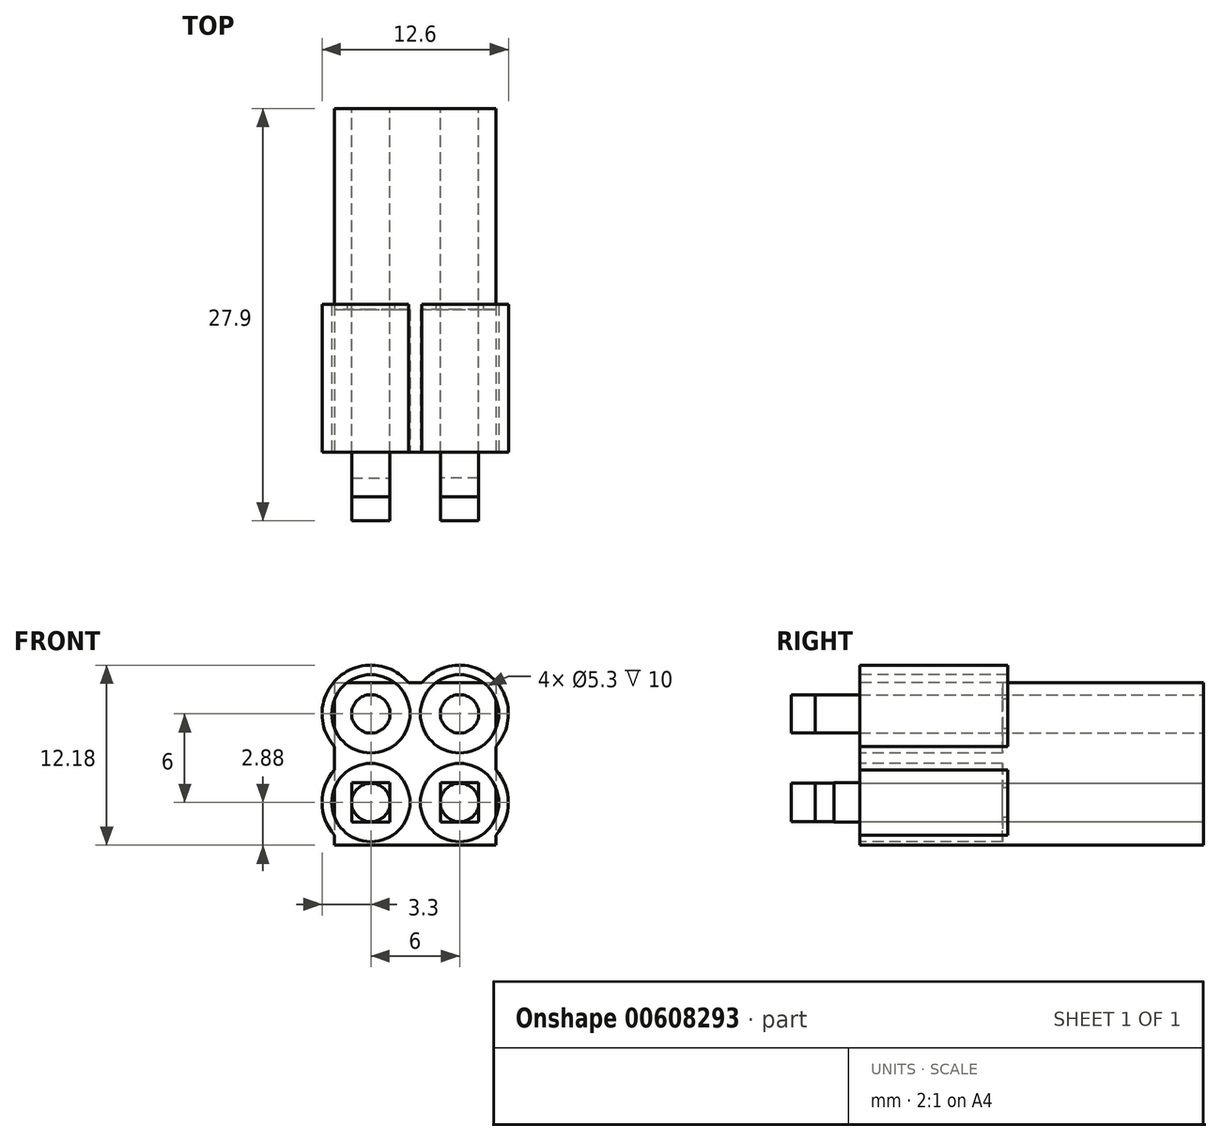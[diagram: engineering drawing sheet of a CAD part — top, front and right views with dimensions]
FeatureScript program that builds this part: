
annotation { "Feature Type Name" : "Feature", "Feature Type Description" : "" }
export const myFeature = defineFeature(function(context is Context, id is Id, definition is map)
    precondition{}
    {
        {
            var Q0;
            Q0=qCreatedBy(makeId("Front.planeOp"),FACE);
            var sketch = newSketch(context, id + "F0", { "sketchPlane" : qUnion([Q0])});
            skLineSegment(sketch, "E0.bottom", {"start": v(-5.45, 6.3) * mm, "end": v(5.45, 6.3) * mm});
            skLineSegment(sketch, "E0.top", {"start": v(-5.45, -6.3) * mm, "end": v(5.45, -6.3) * mm});
            skLineSegment(sketch, "E0.left", {"start": v(-5.45, 6.3) * mm, "end": v(-5.45, -6.3) * mm});
            skLineSegment(sketch, "E0.right", {"start": v(5.45, 6.3) * mm, "end": v(5.45, -6.3) * mm});
            skPoint(sketch, "E0.middle", {"position": v(0, 0) * mm});
            skSolve(sketch);
        }
        {
            var Q0;
            Q0 = qSketchRegion(id + "F0", true);
            extrude(context, id + "F1", {"entities" : qUnion([Q0]), "depth" : 23.26 * mm, "offsetDistance" : 25 * mm});
        }
        {
            var Q0;
            {var subQ0=makeQuery(id+"F7.opExtrude","SWEPT_FACE",FACE,{"disambiguationData":[OSD([sQuery(id+"F6.wireOp",EDGE,"E14")])]});var subQ1=sQuery(id+"F0.wireOp",EDGE,"E0.left");var subQ2=makeQuery(id+"F1.opExtrude","SWEPT_FACE",FACE,{"disambiguationData":[OSD([subQ1])]});var subQ3=sQuery(id+"F0.wireOp",EDGE,"E0.right");var subQ4=makeQuery(id+"F1.opExtrude","SWEPT_FACE",FACE,{"disambiguationData":[OSD([subQ3])]});var subQ5=sQuery(id+"F0.wireOp",EDGE,"E0.bottom");var subQ6=makeQuery(id+"F1.opExtrude","SWEPT_FACE",FACE,{"disambiguationData":[OSD([subQ5])]});var subQ7=makeQuery(id+"F7.opExtrude","SWEPT_FACE",FACE,{"disambiguationData":[OSD([sQuery(id+"F6.wireOp",EDGE,"E15")])]});var subQ8=makeQuery(id+"F1.opExtrude","CAP_FACE",FACE,{"disambiguationData":[OSD([subQ5,sQuery(id+"F0.wireOp",EDGE,"E0.top"),subQ1,subQ3])],"isStart":true});Q0=makeQuery(id+"F9.boolean.opBoolean","MERGE",FACE,{"derivedFrom":[makeQuery(id+"F7.boolean.opBoolean","SPLIT",FACE,{"disambiguationData":[TD([subQ6,subQ2,subQ0])],"derivedFrom":subQ8}),makeQuery(id+"F7.boolean.opBoolean","SPLIT",FACE,{"disambiguationData":[TD([subQ6,subQ4,subQ7])],"derivedFrom":subQ8}),makeQuery(id+"F7.boolean.opBoolean","SPLIT",FACE,{"disambiguationData":[TD([subQ6,subQ2,subQ4,subQ0,subQ7,makeQuery(id+"F7.opExtrude","SWEPT_FACE",FACE,{"disambiguationData":[OSD([sQuery(id+"F6.wireOp",EDGE,"E16")])]}),makeQuery(id+"F7.opExtrude","SWEPT_FACE",FACE,{"disambiguationData":[OSD([sQuery(id+"F6.wireOp",EDGE,"E17")])]}),makeQuery(id+"F7.opExtrude","SWEPT_FACE",FACE,{"disambiguationData":[OSD([sQuery(id+"F6.wireOp",EDGE,"E18.top")])]})])],"derivedFrom":subQ8}),makeQuery(id+"F9.opExtrude","CAP_FACE",FACE,{"disambiguationData":[OSD([sQuery(id+"F8.wireOp",EDGE,"E19.bottom"),sQuery(id+"F8.wireOp",EDGE,"E19.top"),sQuery(id+"F8.wireOp",EDGE,"E19.left"),sQuery(id+"F8.wireOp",EDGE,"E19.right")])],"isStart":true})]});}
            var sketch = newSketch(context, id + "F2", { "sketchPlane" : qUnion([Q0])});
            skLineSegment(sketch, "E1.bottom", {"start": v(-4.3, -0.47) * mm, "end": v(-1.7, -0.47) * mm});
            skLineSegment(sketch, "E1.top", {"start": v(-4.3, -3.13) * mm, "end": v(-1.7, -3.13) * mm});
            skLineSegment(sketch, "E1.left", {"start": v(-4.3, -0.47) * mm, "end": v(-4.3, -3.13) * mm});
            skLineSegment(sketch, "E1.right", {"start": v(-1.7, -0.47) * mm, "end": v(-1.7, -3.13) * mm});
            skPoint(sketch, "E1.middle", {"position": v(-3, -1.8) * mm});
            skLineSegment(sketch, "E2.MirrorCS", {"start": v(4.3, -3.13) * mm, "end": v(1.7, -3.13) * mm});
            skLineSegment(sketch, "E3.MirrorCS", {"start": v(4.3, -0.47) * mm, "end": v(4.3, -3.13) * mm});
            skLineSegment(sketch, "E4.MirrorCS", {"start": v(4.3, -0.47) * mm, "end": v(1.7, -0.47) * mm});
            skLineSegment(sketch, "E5.MirrorCS", {"start": v(1.7, -0.47) * mm, "end": v(1.7, -3.13) * mm});
            skPoint(sketch, "E6.MirrorP", {"position": v(3, -1.8) * mm});
            skSolve(sketch);
        }
        {
            var Q0;
            Q0 = qSketchRegion(id + "F2", true);
            extrude(context, id + "F3", {"entities" : qUnion([Q0]), "oppositeDirection" : true, "depth" : 25 * mm, "offsetDistance" : 25 * mm});
        }
        {
            var Q0;
            Q0=makeQuery(id+"F1.opExtrude","CAP_FACE",FACE,{"disambiguationData":[OSD([sQuery(id+"F0.wireOp",EDGE,"E0.bottom"),sQuery(id+"F0.wireOp",EDGE,"E0.top"),sQuery(id+"F0.wireOp",EDGE,"E0.left"),sQuery(id+"F0.wireOp",EDGE,"E0.right")])],"isStart":false});
            var sketch = newSketch(context, id + "F4", { "sketchPlane" : qUnion([Q0])});
            skArc(sketch, "E7", {"start": v(0, 5.57) * mm, "mid": v(-5.33, 6.53) * mm, "end": v(-4.37, 1.2) * mm});
            skArc(sketch, "E8", {"start": v(4.37, 1.2) * mm, "mid": v(5.33, 6.53) * mm, "end": v(0, 5.57) * mm});
            skLineSegment(sketch, "E9", {"start": v(-3, 4.2) * mm, "end": v(-3, 1.2) * mm});
            skArc(sketch, "E10.MirrorC", {"start": v(-4.37, 1.2) * mm, "mid": v(-5.33, 6.53) * mm, "end": v(0, 5.57) * mm});
            skArc(sketch, "E11.MirrorC", {"start": v(4.37, 1.2) * mm, "mid": v(5.33, -4.13) * mm, "end": v(0, -3.17) * mm});
            skArc(sketch, "E12.trimOffspring", {"start": v(0, -3.17) * mm, "mid": v(-5.33, -4.13) * mm, "end": v(-4.37, 1.2) * mm});
            skPoint(sketch, "E13.end.orphan", {"position": v(-5.45, -1.8) * mm});
            skSolve(sketch);
        }
        {
            var Q0;
            Q0 = qSketchRegion(id + "F4", true);
            extrude(context, id + "F5", {"entities" : qUnion([Q0]), "operationType" : NewBodyOperationType.ADD, "oppositeDirection" : true, "depth" : 10 * mm, "offsetDistance" : 25 * mm});
        }
        {
            var Q0;
            Q0=makeQuery(id+"F5.boolean.opBoolean","MERGE",FACE,{"derivedFrom":[makeQuery(id+"F1.opExtrude","CAP_FACE",FACE,{"disambiguationData":[OSD([sQuery(id+"F0.wireOp",EDGE,"E0.bottom"),sQuery(id+"F0.wireOp",EDGE,"E0.top"),sQuery(id+"F0.wireOp",EDGE,"E0.left"),sQuery(id+"F0.wireOp",EDGE,"E0.right")])],"isStart":false}),makeQuery(id+"F5.opExtrude","CAP_FACE",FACE,{"disambiguationData":[OSD([sQuery(id+"F4.wireOp",EDGE,"E8"),sQuery(id+"F4.wireOp",EDGE,"E10.MirrorC"),sQuery(id+"F4.wireOp",EDGE,"E11.MirrorC"),sQuery(id+"F4.wireOp",EDGE,"E12.trimOffspring")])],"isStart":true})]});
            var sketch = newSketch(context, id + "F6", { "sketchPlane" : qUnion([Q0])});
            skCircle(sketch, "E14", {"center": v(-3, 4.2) * mm, "radius": 2.65 * mm});
            skCircle(sketch, "E15", {"center": v(3, 4.2) * mm, "radius": 2.65 * mm});
            skCircle(sketch, "E16", {"center": v(3, -1.8) * mm, "radius": 2.65 * mm});
            skCircle(sketch, "E17", {"center": v(-3, -1.8) * mm, "radius": 2.65 * mm});
            skLineSegment(sketch, "E18.bottom", {"start": v(5.45, -6.3) * mm, "end": v(-5.45, -6.3) * mm});
            skLineSegment(sketch, "E18.top", {"start": v(5.45, -4.68) * mm, "end": v(-5.45, -4.68) * mm});
            skLineSegment(sketch, "E18.left", {"start": v(5.45, -6.3) * mm, "end": v(5.45, -4.68) * mm});
            skLineSegment(sketch, "E18.right", {"start": v(-5.45, -6.3) * mm, "end": v(-5.45, -4.68) * mm});
            skSolve(sketch);
        }
        {
            var Q0;
            Q0 = qSketchRegion(id + "F6", true);
            extrude(context, id + "F7", {"entities" : qUnion([Q0]), "operationType" : NewBodyOperationType.REMOVE, "endBound" : BoundingType.THROUGH_ALL, "oppositeDirection" : true, "depth" : 25 * mm, "offsetDistance" : 25 * mm});
        }
        {
            var Q0;
            {var subQ0=sQuery(id+"F0.wireOp",EDGE,"E0.left");var subQ1=sQuery(id+"F0.wireOp",EDGE,"E0.right");var subQ2=sQuery(id+"F0.wireOp",EDGE,"E0.bottom");Q0=makeQuery(id+"F7.boolean.opBoolean","SPLIT",FACE,{"disambiguationData":[TD([makeQuery(id+"F1.opExtrude","SWEPT_FACE",FACE,{"disambiguationData":[OSD([subQ2])]}),makeQuery(id+"F1.opExtrude","SWEPT_FACE",FACE,{"disambiguationData":[OSD([subQ0])]}),makeQuery(id+"F1.opExtrude","SWEPT_FACE",FACE,{"disambiguationData":[OSD([subQ1])]}),makeQuery(id+"F7.opExtrude","SWEPT_FACE",FACE,{"disambiguationData":[OSD([sQuery(id+"F6.wireOp",EDGE,"E14")])]}),makeQuery(id+"F7.opExtrude","SWEPT_FACE",FACE,{"disambiguationData":[OSD([sQuery(id+"F6.wireOp",EDGE,"E15")])]}),makeQuery(id+"F7.opExtrude","SWEPT_FACE",FACE,{"disambiguationData":[OSD([sQuery(id+"F6.wireOp",EDGE,"E16")])]}),makeQuery(id+"F7.opExtrude","SWEPT_FACE",FACE,{"disambiguationData":[OSD([sQuery(id+"F6.wireOp",EDGE,"E17")])]}),makeQuery(id+"F7.opExtrude","SWEPT_FACE",FACE,{"disambiguationData":[OSD([sQuery(id+"F6.wireOp",EDGE,"E18.top")])]})])],"derivedFrom":makeQuery(id+"F1.opExtrude","CAP_FACE",FACE,{"disambiguationData":[OSD([subQ2,sQuery(id+"F0.wireOp",EDGE,"E0.top"),subQ0,subQ1])],"isStart":true})});}
            var sketch = newSketch(context, id + "F8", { "sketchPlane" : qUnion([Q0])});
            skLineSegment(sketch, "E19.bottom", {"start": v(5.45, -4.68) * mm, "end": v(-5.45, -4.68) * mm});
            skLineSegment(sketch, "E19.top", {"start": v(5.45, 6.3) * mm, "end": v(-5.45, 6.3) * mm});
            skLineSegment(sketch, "E19.left", {"start": v(5.45, -4.68) * mm, "end": v(5.45, 6.3) * mm});
            skLineSegment(sketch, "E19.right", {"start": v(-5.45, -4.68) * mm, "end": v(-5.45, 6.3) * mm});
            skSolve(sketch);
        }
        {
            var Q0;
            Q0 = qSketchRegion(id + "F8", true);
            extrude(context, id + "F9", {"entities" : qUnion([Q0]), "operationType" : NewBodyOperationType.ADD, "oppositeDirection" : true, "depth" : 13.6 * mm, "offsetDistance" : 25 * mm});
        }
        {
            var Q0;
            Q0=makeQuery(id+"F5.boolean.opBoolean","MERGE",FACE,{"derivedFrom":[makeQuery(id+"F1.opExtrude","CAP_FACE",FACE,{"disambiguationData":[OSD([sQuery(id+"F0.wireOp",EDGE,"E0.bottom"),sQuery(id+"F0.wireOp",EDGE,"E0.top"),sQuery(id+"F0.wireOp",EDGE,"E0.left"),sQuery(id+"F0.wireOp",EDGE,"E0.right")])],"isStart":false}),makeQuery(id+"F5.opExtrude","CAP_FACE",FACE,{"disambiguationData":[OSD([sQuery(id+"F4.wireOp",EDGE,"E8"),sQuery(id+"F4.wireOp",EDGE,"E10.MirrorC"),sQuery(id+"F4.wireOp",EDGE,"E11.MirrorC"),sQuery(id+"F4.wireOp",EDGE,"E12.trimOffspring")])],"isStart":true})]});
            var sketch = newSketch(context, id + "F10", { "sketchPlane" : qUnion([Q0])});
            skPoint(sketch, "E20", {"position": v(-3, -1.8) * mm});
            skCircle(sketch, "E21", {"center": v(-3, -1.8) * mm, "radius": 1.3 * mm});
            skCircle(sketch, "E22", {"center": v(-3, 4.2) * mm, "radius": 1.3 * mm});
            skPoint(sketch, "E23", {"position": v(3, -1.8) * mm});
            skCircle(sketch, "E24", {"center": v(3, -1.8) * mm, "radius": 1.3 * mm});
            skCircle(sketch, "E25", {"center": v(3, 4.2) * mm, "radius": 1.3 * mm});
            skSolve(sketch);
        }
        {
            var Q0;
            Q0 = qSketchRegion(id + "F10", true);
            extrude(context, id + "F11", {"entities" : qUnion([Q0]), "depth" : 3 * mm, "offsetDistance" : 25 * mm});
        }
        {
            var Q0;
            {var subQ0=makeQuery(id+"F7.opExtrude","SWEPT_FACE",FACE,{"disambiguationData":[OSD([sQuery(id+"F6.wireOp",EDGE,"E14")])]});var subQ1=sQuery(id+"F0.wireOp",EDGE,"E0.left");var subQ2=makeQuery(id+"F1.opExtrude","SWEPT_FACE",FACE,{"disambiguationData":[OSD([subQ1])]});var subQ3=sQuery(id+"F0.wireOp",EDGE,"E0.right");var subQ4=makeQuery(id+"F1.opExtrude","SWEPT_FACE",FACE,{"disambiguationData":[OSD([subQ3])]});var subQ5=sQuery(id+"F0.wireOp",EDGE,"E0.bottom");var subQ6=makeQuery(id+"F1.opExtrude","SWEPT_FACE",FACE,{"disambiguationData":[OSD([subQ5])]});var subQ7=makeQuery(id+"F7.opExtrude","SWEPT_FACE",FACE,{"disambiguationData":[OSD([sQuery(id+"F6.wireOp",EDGE,"E15")])]});var subQ8=makeQuery(id+"F1.opExtrude","CAP_FACE",FACE,{"disambiguationData":[OSD([subQ5,sQuery(id+"F0.wireOp",EDGE,"E0.top"),subQ1,subQ3])],"isStart":true});Q0=makeQuery(id+"F9.boolean.opBoolean","MERGE",FACE,{"derivedFrom":[makeQuery(id+"F7.boolean.opBoolean","SPLIT",FACE,{"disambiguationData":[TD([subQ6,subQ2,subQ0])],"derivedFrom":subQ8}),makeQuery(id+"F7.boolean.opBoolean","SPLIT",FACE,{"disambiguationData":[TD([subQ6,subQ4,subQ7])],"derivedFrom":subQ8}),makeQuery(id+"F7.boolean.opBoolean","SPLIT",FACE,{"disambiguationData":[TD([subQ6,subQ2,subQ4,subQ0,subQ7,makeQuery(id+"F7.opExtrude","SWEPT_FACE",FACE,{"disambiguationData":[OSD([sQuery(id+"F6.wireOp",EDGE,"E16")])]}),makeQuery(id+"F7.opExtrude","SWEPT_FACE",FACE,{"disambiguationData":[OSD([sQuery(id+"F6.wireOp",EDGE,"E17")])]}),makeQuery(id+"F7.opExtrude","SWEPT_FACE",FACE,{"disambiguationData":[OSD([sQuery(id+"F6.wireOp",EDGE,"E18.top")])]})])],"derivedFrom":subQ8}),makeQuery(id+"F9.opExtrude","CAP_FACE",FACE,{"disambiguationData":[OSD([sQuery(id+"F8.wireOp",EDGE,"E19.bottom"),sQuery(id+"F8.wireOp",EDGE,"E19.top"),sQuery(id+"F8.wireOp",EDGE,"E19.left"),sQuery(id+"F8.wireOp",EDGE,"E19.right")])],"isStart":true})]});}
            var sketch = newSketch(context, id + "F12", { "sketchPlane" : qUnion([Q0])});
            skCircle(sketch, "E26.0", {"center": v(3, 4.2) * mm, "radius": 1.3 * mm});
            skCircle(sketch, "E27.0", {"center": v(-3, 4.2) * mm, "radius": 1.3 * mm});
            skCircle(sketch, "E28.0", {"center": v(-3, -1.8) * mm, "radius": 1.3 * mm});
            skCircle(sketch, "E29.0", {"center": v(3, -1.8) * mm, "radius": 1.3 * mm});
            skSolve(sketch);
        }
        {
            var Q0;
            Q0 = qSketchRegion(id + "F12", true);
            var Q1;
            Q1=makeQuery(id+"F11.opExtrude","CAP_FACE",FACE,{"disambiguationData":[OSD([sQuery(id+"F10.wireOp",EDGE,"E22")])],"isStart":false});
            extrude(context, id + "F13", {"entities" : qUnion([Q0]), "oppositeDirection" : true, "depth" : 27.9 * mm, "endBoundEntityFace" : qUnion([Q1]), "offsetDistance" : 25 * mm});
        }
    });
